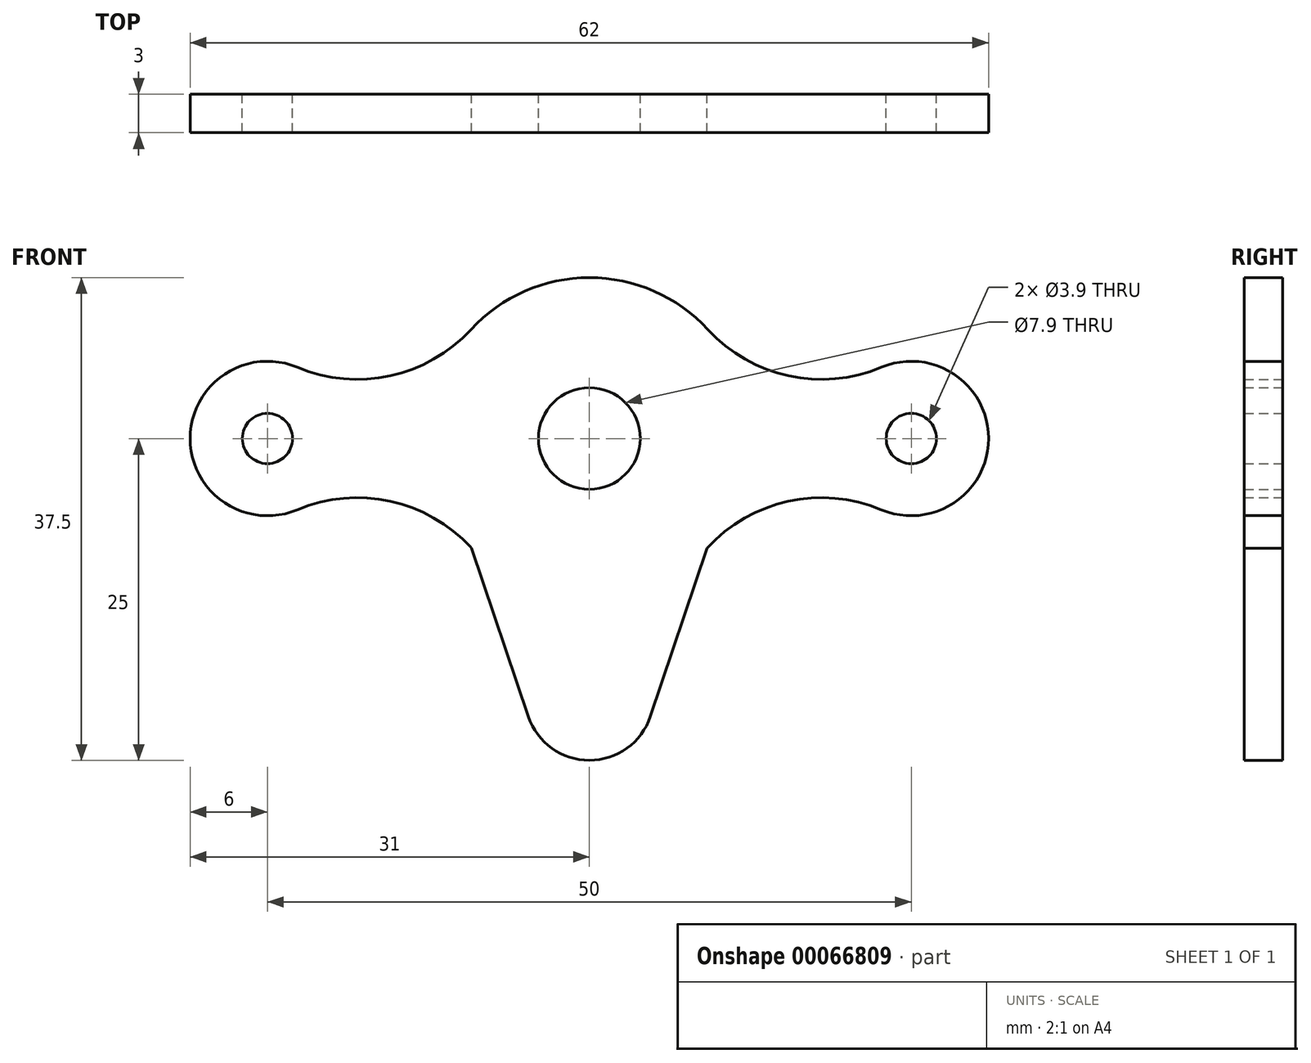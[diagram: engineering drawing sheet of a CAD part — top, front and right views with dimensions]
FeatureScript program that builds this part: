
annotation { "Feature Type Name" : "Feature", "Feature Type Description" : "" }
export const myFeature = defineFeature(function(context is Context, id is Id, definition is map)
    precondition{}
    {
        {
            var Q0;
            Q0=qCreatedBy(makeId("Front.planeOp"),FACE);
            var sketch = newSketch(context, id + "F0", { "sketchPlane" : qUnion([Q0])});
            skCircle(sketch, "E0", {"center": v(0, 0) * mm, "radius": 3.95 * mm});
            skArc(sketch, "E1", {"start": v(-9.2, -8.47) * mm, "mid": v(-9.17, -8.5) * mm, "end": v(-9.14, -8.52) * mm});
            skLineSegment(sketch, "E2", {"start": v(0, 0) * mm, "end": v(0, 15.73) * mm});
            skLineSegment(sketch, "E3", {"start": v(-25, 15.73) * mm, "end": v(-25, -4.65) * mm});
            skArc(sketch, "E4", {"start": v(-22.68, 5.53) * mm, "mid": v(-31, 0) * mm, "end": v(-22.68, -5.53) * mm});
            skCircle(sketch, "E5", {"center": v(-25, 0) * mm, "radius": 1.95 * mm});
            skArc(sketch, "E6", {"start": v(-9.15, -8.52) * mm, "mid": v(-9.15, -8.52) * mm, "end": v(-9.14, -8.52) * mm});
            skArc(sketch, "E7", {"start": v(-9.15, -8.52) * mm, "mid": v(-16.02, -4.76) * mm, "end": v(-23.74, -6.04) * mm});
            skArc(sketch, "E8.MirrorCS", {"start": v(-9.15, 8.52) * mm, "mid": v(-16.02, 4.76) * mm, "end": v(-23.74, 6.04) * mm});
            skArc(sketch, "E9.trimOffspring", {"start": v(-23.79, -5.88) * mm, "mid": v(-23.76, -5.96) * mm, "end": v(-23.74, -6.04) * mm});
            skArc(sketch, "E10.MirrorCS", {"start": v(9.15, 8.52) * mm, "mid": v(16.02, 4.76) * mm, "end": v(23.74, 6.04) * mm});
            skArc(sketch, "E11.MirrorC", {"start": v(22.68, 5.53) * mm, "mid": v(31, 0) * mm, "end": v(22.68, -5.53) * mm});
            skCircle(sketch, "E12.MirrorC", {"center": v(25, 0) * mm, "radius": 1.95 * mm});
            skArc(sketch, "E13.MirrorCS", {"start": v(9.15, -8.52) * mm, "mid": v(16.02, -4.76) * mm, "end": v(23.74, -6.04) * mm});
            skArc(sketch, "E14.trimOffspring", {"start": v(9.2, 8.47) * mm, "mid": v(0, 12.5) * mm, "end": v(-9.2, 8.47) * mm});
            skArc(sketch, "E15", {"start": v(-4.74, -21.6) * mm, "mid": v(0, -25) * mm, "end": v(4.74, -21.6) * mm});
            skLineSegment(sketch, "E16", {"start": v(9.15, -8.52) * mm, "end": v(4.74, -21.6) * mm});
            skLineSegment(sketch, "E17.MirrorCS", {"start": v(-9.15, -8.52) * mm, "end": v(-4.74, -21.6) * mm});
            skSolve(sketch);
        }
        {
            var Q0;
            Q0=makeQuery(id+"F0.imprint","IMPRINT",FACE,{"disambiguationData":[TD([[makeQuery(id+"F0.imprint","IMPRINT",EDGE,{"derivedFrom":sQuery(id+"F0.wireOp",EDGE,"E0")}),-1.0]])]});
            extrude(context, id + "F1", {"entities" : qUnion([Q0]), "depth" : 3 * mm});
        }
    });
